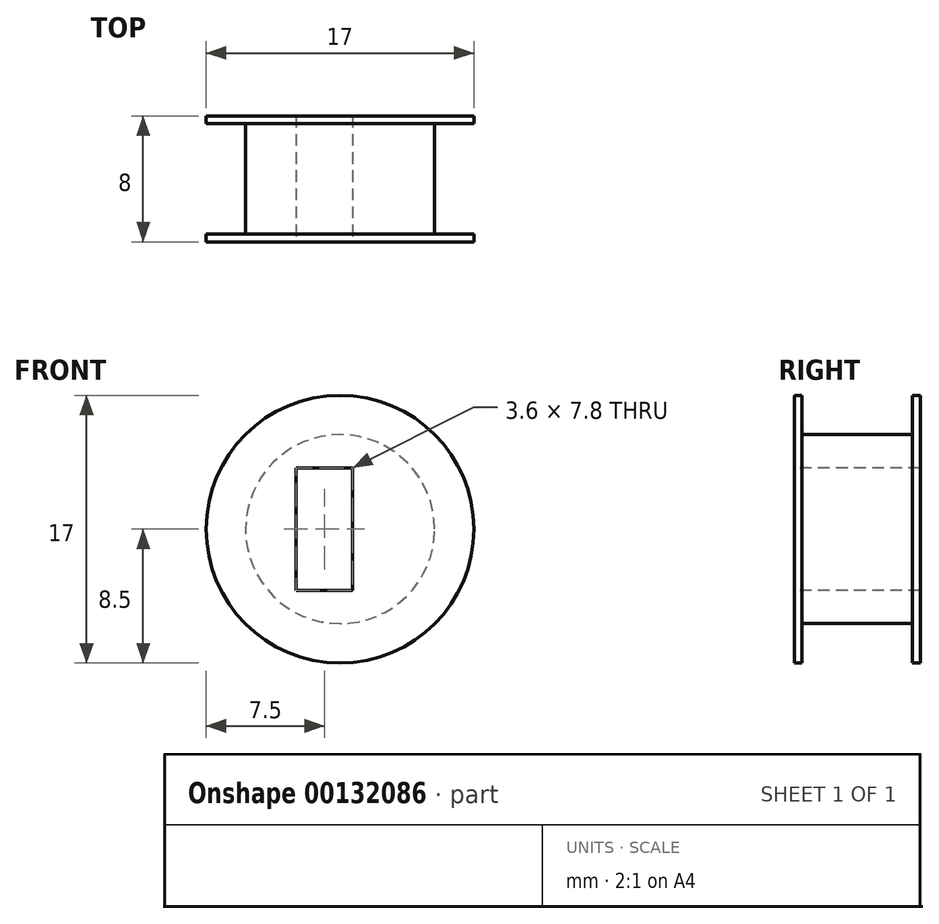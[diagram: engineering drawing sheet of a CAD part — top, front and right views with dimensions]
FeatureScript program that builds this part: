
annotation { "Feature Type Name" : "Feature", "Feature Type Description" : "" }
export const myFeature = defineFeature(function(context is Context, id is Id, definition is map)
    precondition{}
    {
        {
            var Q0;
            Q0=qCreatedBy(makeId("Front.planeOp"),FACE);
            var sketch = newSketch(context, id + "F0", { "sketchPlane" : qUnion([Q0])});
            skCircle(sketch, "E0", {"center": v(0, 0) * mm, "radius": 8.5 * mm});
            skSolve(sketch);
        }
        {
            var Q0;
            Q0=makeQuery(id+"F0.imprint","IMPRINT",FACE,{"disambiguationData":[TD([[makeQuery(id+"F0.imprint","IMPRINT",EDGE,{"derivedFrom":sQuery(id+"F0.wireOp",EDGE,"E0")}),1.0]])]});
            extrude(context, id + "F1", {"entities" : qUnion([Q0]), "depth" : 8 * mm});
        }
        {
            var Q0;
            Q0=makeQuery(id+"F1.opExtrude","CAP_FACE",FACE,{"disambiguationData":[OSD([sQuery(id+"F0.wireOp",EDGE,"E0")])],"isStart":false});
            var sketch = newSketch(context, id + "F2", { "sketchPlane" : qUnion([Q0])});
            skLineSegment(sketch, "E1.bottom", {"start": v(-2.8, 3.9) * mm, "end": v(0.8, 3.9) * mm});
            skLineSegment(sketch, "E1.top", {"start": v(-2.8, -3.9) * mm, "end": v(0.8, -3.9) * mm});
            skLineSegment(sketch, "E1.left", {"start": v(-2.8, 3.9) * mm, "end": v(-2.8, -3.9) * mm});
            skLineSegment(sketch, "E1.right", {"start": v(0.8, 3.9) * mm, "end": v(0.8, -3.9) * mm});
            skSolve(sketch);
        }
        {
            var Q0;
            Q0=makeQuery(id+"F2.imprint","IMPRINT",FACE,{"disambiguationData":[TD([[makeQuery(id+"F2.imprint","IMPRINT",EDGE,{"derivedFrom":sQuery(id+"F2.wireOp",EDGE,"E1.bottom")}),-1.0]])]});
            extrude(context, id + "F3", {"entities" : qUnion([Q0]), "operationType" : NewBodyOperationType.REMOVE, "oppositeDirection" : true, "depth" : 8 * mm});
        }
        {
            var Q0;
            {var subQ0=sQuery(id+"F0.wireOp",EDGE,"E0");Q0=makeQuery(id+"FTi8eRQbPzAKgnm_1.boolean.opBoolean","MERGE",FACE,{"derivedFrom":[makeQuery(id+"F1.opExtrude","CAP_FACE",FACE,{"disambiguationData":[OSD([subQ0])],"isStart":false}),makeQuery(id+"FTi8eRQbPzAKgnm_1.opExtrude","CAP_FACE",FACE,{"disambiguationData":[OSD([subQ0,sQuery(id+"Fsbxnbc9it0xA0t_1.wireOp",EDGE,"z3zPwZlD-sBK9-szPG-YAd1-iPIMpAxUMSGT")])],"isStart":true})]});}
            var sketch = newSketch(context, id + "F4", { "sketchPlane" : qUnion([Q0])});
            skCircle(sketch, "E2", {"center": v(0, 0) * mm, "radius": 8.5 * mm});
            skCircle(sketch, "E3", {"center": v(0, 0) * mm, "radius": 6 * mm});
            skSolve(sketch);
        }
        {
            var Q0;
            Q0=makeQuery(id+"F4.imprint","IMPRINT",FACE,{"disambiguationData":[TD([[makeQuery(id+"F4.imprint","IMPRINT",EDGE,{"derivedFrom":sQuery(id+"F4.wireOp",EDGE,"E2")}),1.0]])]});
            extrude(context, id + "F5", {"entities" : qUnion([Q0]), "operationType" : NewBodyOperationType.REMOVE, "oppositeDirection" : true, "depth" : 7.5 * mm});
        }
        {
            var Q0;
            {var subQ0=sQuery(id+"F0.wireOp",EDGE,"E0");Q0=makeQuery(id+"FTi8eRQbPzAKgnm_1.boolean.opBoolean","MERGE",FACE,{"derivedFrom":[makeQuery(id+"F1.opExtrude","CAP_FACE",FACE,{"disambiguationData":[OSD([subQ0])],"isStart":false}),makeQuery(id+"FTi8eRQbPzAKgnm_1.opExtrude","CAP_FACE",FACE,{"disambiguationData":[OSD([subQ0,sQuery(id+"Fsbxnbc9it0xA0t_1.wireOp",EDGE,"z3zPwZlD-sBK9-szPG-YAd1-iPIMpAxUMSGT")])],"isStart":true})]});}
            var sketch = newSketch(context, id + "F6", { "sketchPlane" : qUnion([Q0])});
            skCircle(sketch, "E4", {"center": v(0, 0) * mm, "radius": 8.5 * mm});
            skSolve(sketch);
        }
        {
            var Q0;
            Q0=makeQuery(id+"F6.imprint","IMPRINT",FACE,{"disambiguationData":[TD([[makeQuery(id+"F6.imprint","IMPRINT",EDGE,{"derivedFrom":sQuery(id+"F6.wireOp",EDGE,"E4")}),1.0]])]});
            extrude(context, id + "F7", {"entities" : qUnion([Q0]), "operationType" : NewBodyOperationType.ADD, "oppositeDirection" : true, "depth" : 0.5 * mm});
        }
    });
